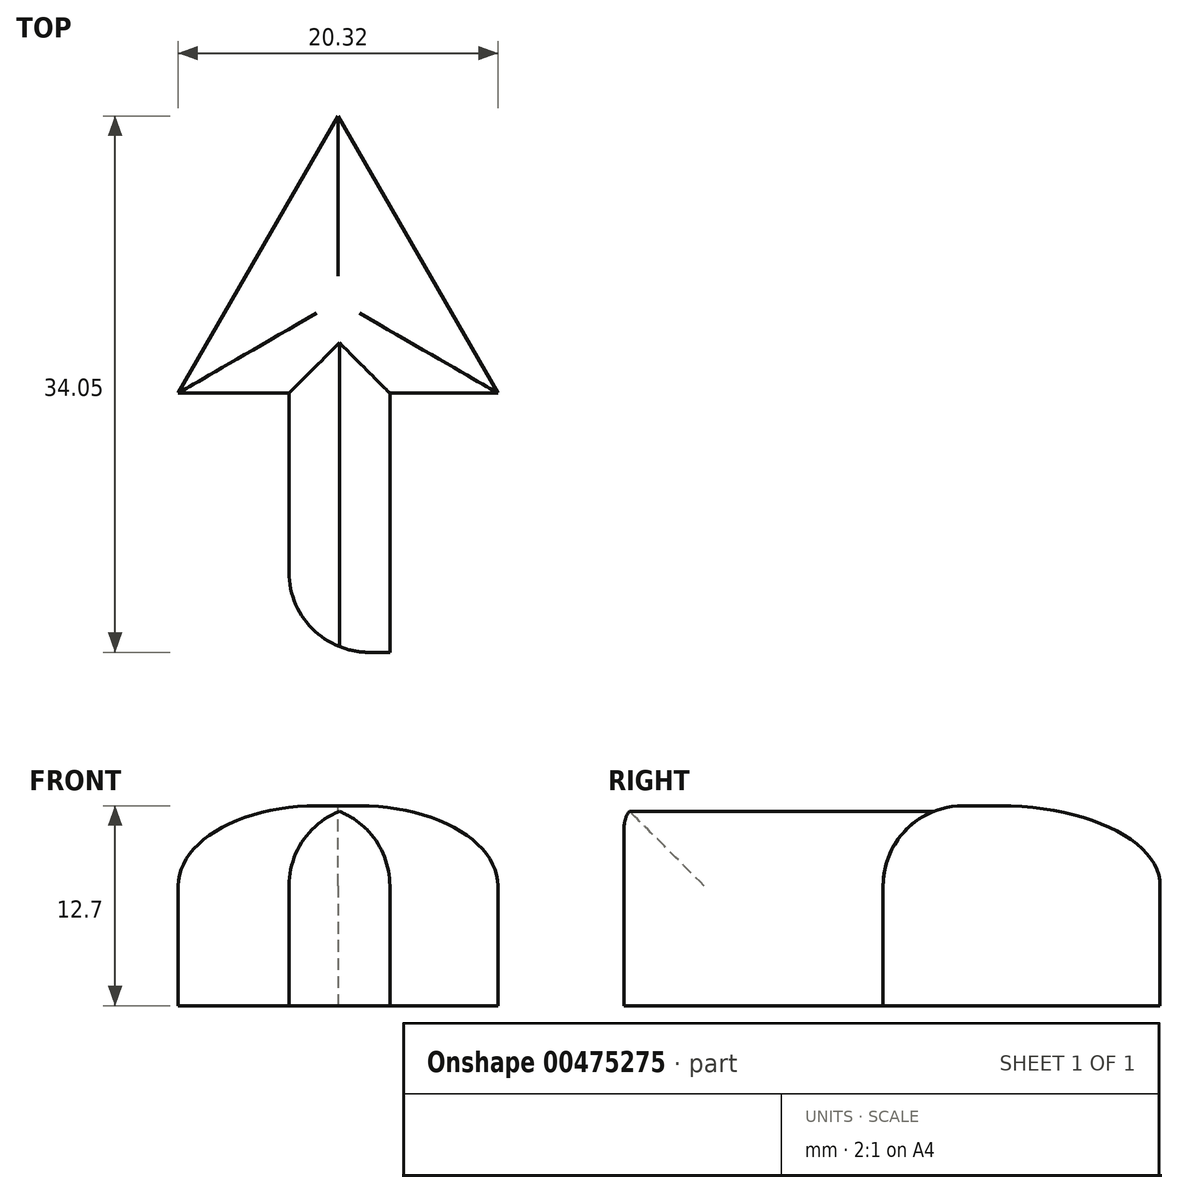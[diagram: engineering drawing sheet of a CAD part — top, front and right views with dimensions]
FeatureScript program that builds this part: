
annotation { "Feature Type Name" : "Feature", "Feature Type Description" : "" }
export const myFeature = defineFeature(function(context is Context, id is Id, definition is map)
    precondition{}
    {
        {
            var Q0;
            Q0=qCreatedBy(makeId("Top.planeOp"),FACE);
            var sketch = newSketch(context, id + "F0", { "sketchPlane" : qUnion([Q0])});
            skLineSegment(sketch, "E0", {"start": v(-48.7, 29.33) * mm, "end": v(-58.86, 11.73) * mm});
            skLineSegment(sketch, "E1", {"start": v(-58.86, 11.73) * mm, "end": v(-38.54, 11.73) * mm});
            skLineSegment(sketch, "E2", {"start": v(-38.54, 11.73) * mm, "end": v(-48.7, 29.33) * mm});
            skSolve(sketch);
        }
        {
            var Q0;
            Q0=makeQuery(id+"F0.imprint","IMPRINT",FACE,{"disambiguationData":[TD([[makeQuery(id+"F0.imprint","IMPRINT",EDGE,{"derivedFrom":sQuery(id+"F0.wireOp",EDGE,"E0")}),1.0]])]});
            extrude(context, id + "F1", {"entities" : qUnion([Q0]), "depth" : 12.7 * mm});
        }
        {
            var Q0;
            Q0=qCreatedBy(makeId("Top.planeOp"),FACE);
            var sketch = newSketch(context, id + "F2", { "sketchPlane" : qUnion([Q0])});
            skLineSegment(sketch, "E3.bottom", {"start": v(-51.82, 12.04) * mm, "end": v(-45.42, 12.04) * mm});
            skLineSegment(sketch, "E3.top", {"start": v(-51.82, -4.72) * mm, "end": v(-45.42, -4.72) * mm});
            skLineSegment(sketch, "E3.left", {"start": v(-51.82, 12.04) * mm, "end": v(-51.82, -4.72) * mm});
            skLineSegment(sketch, "E3.right", {"start": v(-45.42, 12.04) * mm, "end": v(-45.42, -4.72) * mm});
            skSolve(sketch);
        }
        {
            var Q0;
            Q0=makeQuery(id+"F2.imprint","IMPRINT",FACE,{"disambiguationData":[TD([[makeQuery(id+"F2.imprint","IMPRINT",EDGE,{"derivedFrom":sQuery(id+"F2.wireOp",EDGE,"E3.bottom")}),-1.0]])]});
            extrude(context, id + "F3", {"entities" : qUnion([Q0]), "operationType" : NewBodyOperationType.ADD, "depth" : 12.7 * mm});
        }
        {
            var Q0;
            {var subQ1=sQuery(id+"F0.wireOp",EDGE,"E1");var subQ2=sQuery(id+"F0.wireOp",EDGE,"E2");Q0=makeQuery(id+"F3.boolean.opBoolean","SPLIT",EDGE,{"disambiguationData":[TD([makeQuery(id+"F1.opExtrude","SWEPT_FACE",FACE,{"disambiguationData":[OSD([subQ2])]})])],"derivedFrom":makeQuery(id+"F1.opExtrude","CAP_EDGE",EDGE,{"disambiguationData":[OSD([subQ1])],"isStart":false})});}
            var Q1;
            {var subQ0=sQuery(id+"F0.wireOp",EDGE,"E1");var subQ2=sQuery(id+"F0.wireOp",EDGE,"E0");Q1=makeQuery(id+"F3.boolean.opBoolean","SPLIT",EDGE,{"disambiguationData":[TD([makeQuery(id+"F1.opExtrude","SWEPT_FACE",FACE,{"disambiguationData":[OSD([subQ2])]})])],"derivedFrom":makeQuery(id+"F1.opExtrude","CAP_EDGE",EDGE,{"disambiguationData":[OSD([subQ0])],"isStart":false})});}
            var Q2;
            Q2=makeQuery(id+"F3.opExtrude","CAP_EDGE",EDGE,{"disambiguationData":[OSD([sQuery(id+"F2.wireOp",EDGE,"E3.right")])],"isStart":false});
            var Q3;
            Q3=makeQuery(id+"F3.opExtrude","CAP_EDGE",EDGE,{"disambiguationData":[OSD([sQuery(id+"F2.wireOp",EDGE,"E3.left")])],"isStart":false});
            fillet(context, id + "F4", {"entities" : qUnion([Q0, Q1, Q2, Q3]), "radius" : 5.08 * mm, "tangentPropagation" : true, "allowEdgeOverflow" : false});
        }
        {
            var Q0;
            Q0=makeQuery(id+"F1.opExtrude","CAP_EDGE",EDGE,{"disambiguationData":[OSD([sQuery(id+"F0.wireOp",EDGE,"E0")])],"isStart":false});
            var Q1;
            Q1=makeQuery(id+"F1.opExtrude","CAP_EDGE",EDGE,{"disambiguationData":[OSD([sQuery(id+"F0.wireOp",EDGE,"E2")])],"isStart":false});
            fillet(context, id + "F5", {"entities" : qUnion([Q0, Q1]), "radius" : 5.08 * mm, "tangentPropagation" : true, "allowEdgeOverflow" : false});
        }
        {
            var Q0;
            Q0=makeQuery(id+"F4.opFillet","BLEND_EDGE",EDGE,{"blendedFrom":[makeQuery(id+"F3.opExtrude","CAP_EDGE",EDGE,{"disambiguationData":[OSD([sQuery(id+"F2.wireOp",EDGE,"E3.left")])],"isStart":false}),makeQuery(id+"F3.opExtrude","SWEPT_FACE",FACE,{"disambiguationData":[OSD([sQuery(id+"F2.wireOp",EDGE,"E3.top")])]})],"blendedInto":[makeQuery(id+"F3.opExtrude","SWEPT_FACE",FACE,{"disambiguationData":[OSD([sQuery(id+"F2.wireOp",EDGE,"E3.top")])]})]});
            fillet(context, id + "F6", {"entities" : qUnion([Q0]), "radius" : 5.08 * mm, "tangentPropagation" : true, "allowEdgeOverflow" : false});
        }
    });
